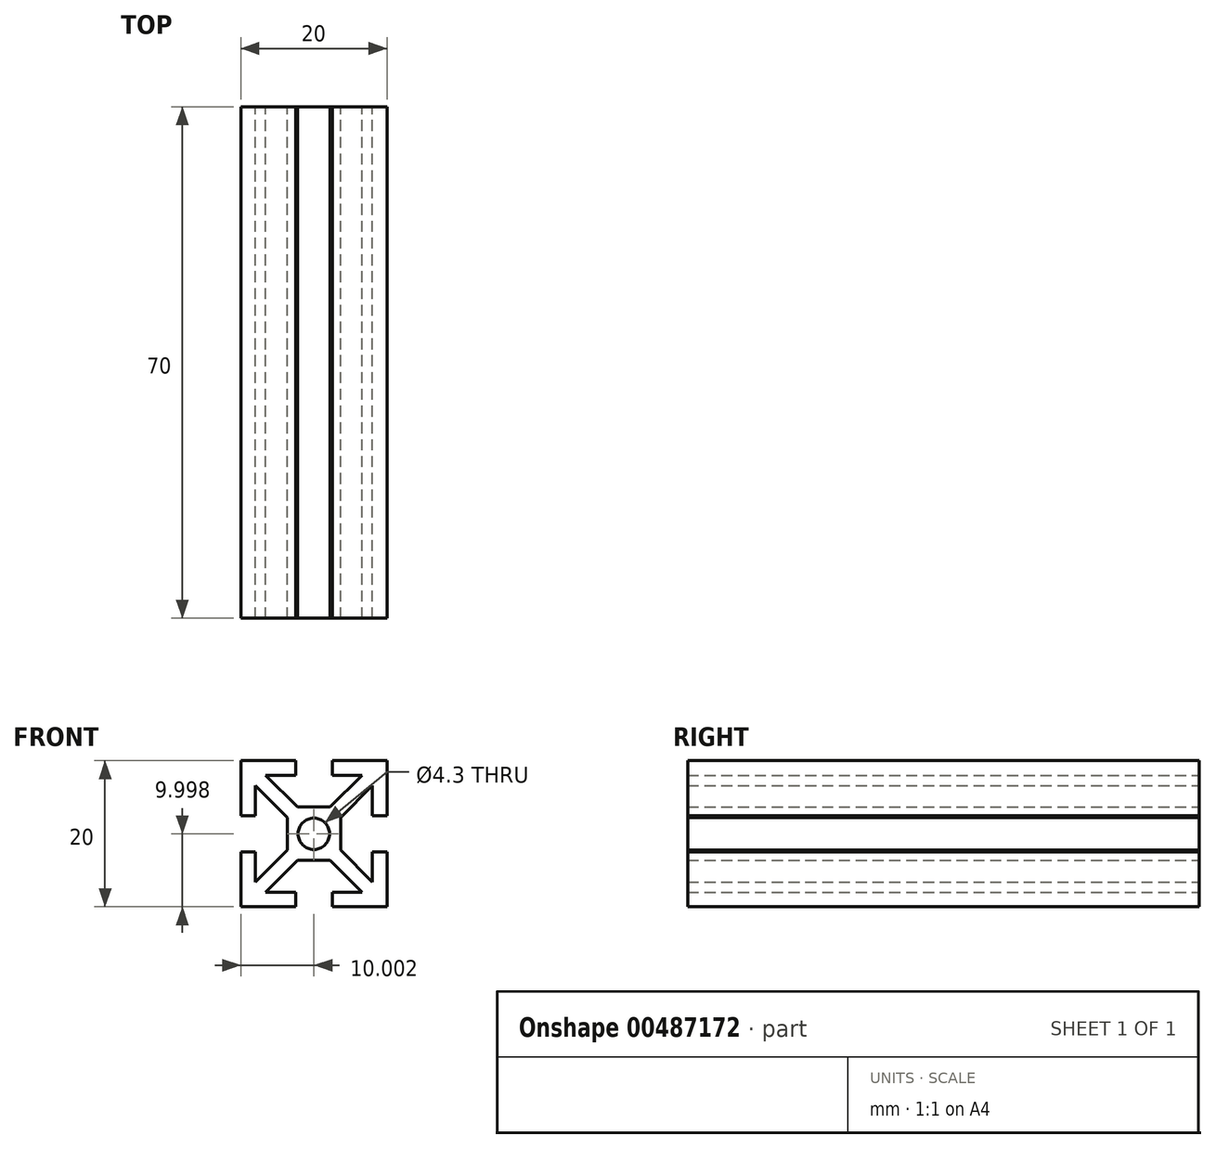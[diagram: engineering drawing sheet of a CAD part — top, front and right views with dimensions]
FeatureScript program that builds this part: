
annotation { "Feature Type Name" : "Feature", "Feature Type Description" : "" }
export const myFeature = defineFeature(function(context is Context, id is Id, definition is map)
    precondition{}
    {
        {
            var Q0;
            Q0=qCreatedBy(makeId("Front.planeOp"),FACE);
            var sketch = newSketch(context, id + "F0", { "sketchPlane" : qUnion([Q0])});
            skLineSegment(sketch, "E0.bottom", {"start": v(-9.74, 9.77) * mm, "end": v(-2.24, 9.77) * mm});
            skLineSegment(sketch, "E0.left", {"start": v(-9.74, 9.77) * mm, "end": v(-9.74, 2.27) * mm});
            skLineSegment(sketch, "E0.right", {"start": v(10.26, 9.77) * mm, "end": v(10.26, 2.27) * mm});
            skArc(sketch, "E1", {"start": v(2.41, -0.23) * mm, "mid": v(0.26, 1.92) * mm, "end": v(-1.89, -0.23) * mm});
            skLineSegment(sketch, "E2.bottom", {"start": v(-1.97, 3.42) * mm, "end": v(2.5, 3.42) * mm});
            skLineSegment(sketch, "E2.left", {"start": v(-3.39, 2) * mm, "end": v(-3.39, -0.23) * mm});
            skLineSegment(sketch, "E2.right", {"start": v(3.91, 2) * mm, "end": v(3.91, -0.23) * mm});
            skLineSegment(sketch, "E3", {"start": v(-2.24, 9.77) * mm, "end": v(-2.24, 7.77) * mm});
            skLineSegment(sketch, "E4", {"start": v(-2.24, 7.77) * mm, "end": v(-6.32, 7.77) * mm});
            skLineSegment(sketch, "E5", {"start": v(2.76, 9.77) * mm, "end": v(2.76, 7.77) * mm});
            skPoint(sketch, "E5.endSnap0", {"position": v(-5.99, 7.77) * mm});
            skLineSegment(sketch, "E6", {"start": v(2.76, 7.77) * mm, "end": v(6.85, 7.77) * mm});
            skLineSegment(sketch, "E7", {"start": v(-7.74, 6.35) * mm, "end": v(-7.74, 2.27) * mm});
            skLineSegment(sketch, "E8", {"start": v(-7.74, 2.27) * mm, "end": v(-9.74, 2.27) * mm});
            skLineSegment(sketch, "E9", {"start": v(-7.74, 6.35) * mm, "end": v(-3.39, 2) * mm});
            skLineSegment(sketch, "E10", {"start": v(-1.97, 3.42) * mm, "end": v(-6.32, 7.77) * mm});
            skPoint(sketch, "E10.endSnap0", {"position": v(-6.32, -0.18) * mm});
            skLineSegment(sketch, "E11", {"start": v(8.26, 6.35) * mm, "end": v(8.26, 2.27) * mm});
            skLineSegment(sketch, "E12", {"start": v(8.26, 2.27) * mm, "end": v(10.26, 2.27) * mm});
            skPoint(sketch, "E13.orphan", {"position": v(10.26, 7.77) * mm});
            skLineSegment(sketch, "E14", {"start": v(2.5, 3.42) * mm, "end": v(6.85, 7.77) * mm});
            skLineSegment(sketch, "E15", {"start": v(3.91, 2) * mm, "end": v(8.26, 6.35) * mm});
            skPoint(sketch, "E16.orphan", {"position": v(-9.74, 7.77) * mm});
            skPoint(sketch, "E17.orphan", {"position": v(-3.39, 3.42) * mm});
            skPoint(sketch, "E18.orphan", {"position": v(3.91, 3.42) * mm});
            skLineSegment(sketch, "E19", {"start": v(-9.74, -0.23) * mm, "end": v(10.26, -0.23) * mm, "construction": true});
            skPoint(sketch, "E0.top.end.orphan", {"position": v(10.26, -10.23) * mm});
            skPoint(sketch, "E0.top.start.orphan", {"position": v(-9.74, -10.23) * mm});
            skLineSegment(sketch, "E20.MirrorCS", {"start": v(-9.74, -10.23) * mm, "end": v(-9.74, -2.73) * mm});
            skLineSegment(sketch, "E21.MirrorCS", {"start": v(-7.74, -2.73) * mm, "end": v(-9.74, -2.73) * mm});
            skLineSegment(sketch, "E22.MirrorCS", {"start": v(-7.74, -6.82) * mm, "end": v(-7.74, -2.73) * mm});
            skLineSegment(sketch, "E23.MirrorCS", {"start": v(-7.74, -6.82) * mm, "end": v(-3.39, -2.47) * mm});
            skLineSegment(sketch, "E24.MirrorCS", {"start": v(-3.39, -2.47) * mm, "end": v(-3.39, -0.23) * mm});
            skArc(sketch, "E25.MirrorCS", {"start": v(2.41, -0.23) * mm, "mid": v(0.26, -2.38) * mm, "end": v(-1.89, -0.23) * mm});
            skLineSegment(sketch, "E26.MirrorCS", {"start": v(-1.97, -3.88) * mm, "end": v(-6.32, -8.23) * mm});
            skLineSegment(sketch, "E27.MirrorCS", {"start": v(-1.97, -3.88) * mm, "end": v(2.5, -3.88) * mm});
            skLineSegment(sketch, "E28.MirrorCS", {"start": v(-2.24, -8.23) * mm, "end": v(-6.32, -8.23) * mm});
            skLineSegment(sketch, "E29.MirrorCS", {"start": v(-2.24, -10.23) * mm, "end": v(-2.24, -8.23) * mm});
            skLineSegment(sketch, "E30.MirrorCS", {"start": v(-9.74, -10.23) * mm, "end": v(-2.24, -10.23) * mm});
            skLineSegment(sketch, "E31.MirrorCS", {"start": v(2.76, -10.23) * mm, "end": v(2.76, -8.23) * mm});
            skLineSegment(sketch, "E32.MirrorCS", {"start": v(2.76, -8.23) * mm, "end": v(6.85, -8.23) * mm});
            skLineSegment(sketch, "E33.MirrorCS", {"start": v(2.5, -3.88) * mm, "end": v(6.85, -8.23) * mm});
            skLineSegment(sketch, "E34.MirrorCS", {"start": v(3.91, -2.47) * mm, "end": v(8.26, -6.82) * mm});
            skLineSegment(sketch, "E35.MirrorCS", {"start": v(8.26, -6.82) * mm, "end": v(8.26, -2.73) * mm});
            skLineSegment(sketch, "E36.MirrorCS", {"start": v(8.26, -2.73) * mm, "end": v(10.26, -2.73) * mm});
            skLineSegment(sketch, "E37.MirrorCS", {"start": v(10.26, -10.23) * mm, "end": v(10.26, -2.73) * mm});
            skLineSegment(sketch, "E38.MirrorCS", {"start": v(3.91, -2.47) * mm, "end": v(3.91, -0.23) * mm});
            skLineSegment(sketch, "E39.trimOffspring", {"start": v(2.76, 9.77) * mm, "end": v(10.26, 9.77) * mm});
            skLineSegment(sketch, "E40.trimOffspring", {"start": v(2.76, -10.23) * mm, "end": v(10.26, -10.23) * mm});
            skSolve(sketch);
        }
        {
            var Q0;
            Q0 = qSketchRegion(id + "F0", true);
            extrude(context, id + "F1", {"entities" : qUnion([Q0]), "depth" : 35 * mm, "hasSecondDirection" : true, "secondDirectionOppositeDirection" : true, "secondDirectionDepth" : 35 * mm});
        }
    });
